MODEL slx_324b0836d6e7
KIND model
CONFIG AbsTol = auto
CONFIG EnableMultiTasking = on
CONFIG FixedStep = tS
CONFIG MaxStep = auto
CONFIG MinStep = auto
CONFIG RelTol = 1e-3
CONFIG SampleTimeConstraint = Unconstrained
CONFIG Solver = ode2
CONFIG SolverName = ode2
CONFIG StartTime = 0.0
CONFIG StopTime = inf
WORKSPACE source: MAT-file member
WORKSPACE m = 1000
BLOCK [BusSelector] Bus Selector
  OutputAsBus = off
  OutputSignals = RequestSteeringAngle_rad,RequestLongForce_N,RequestThrottle_perc,RequestBrake_bar,RequestGear
  Ports = [1, 5]
BLOCK [ModelReference] Model
  ModelNameDialog = debug_conversion_debug.slx
  ModelReferenceVersion = 1.8
  Ports = [1, 1]
BLOCK [ModelReference] Model1
  ModelNameDialog = debug_conversion_debug_slow.slx
  ModelReferenceVersion = 1.8
  Ports = [1, 1]
BLOCK [Terminator] Terminator
BLOCK [Terminator] Terminator1
BLOCK [Inport] in_ActuatorLimitations
  IconDisplay = Port number
  OutDataTypeStr = Bus: ActuatorLimitations
  Port = 4
BLOCK [Inport] in_ExternalDebug
  IconDisplay = Port number
  OutDataTypeStr = Bus: ExternalDebug
  Port = 5
BLOCK [Inport] in_TrajectoryPlanning
  IconDisplay = Port number
  OutDataTypeStr = Bus: TrajectoryPlanning
BLOCK [Inport] in_VehicleSensorData
  IconDisplay = Port number
  OutDataTypeStr = Bus: VehicleSensorData
  Port = 2
BLOCK [Inport] in_VehicleSystemStatus
  IconDisplay = Port number
  OutDataTypeStr = Bus: VehicleSystemStatus
  Port = 3
BLOCK [ModelReference] mvdc_vehicle_dynamics_control1
  ModelNameDialog = mvdc_vehicle_dynamics_control
  ModelReferenceVersion = 1.801
  Ports = [5, 8]
BLOCK [Outport] out_BrakePressure_bar
  IconDisplay = Port number
  Port = 9
BLOCK [Outport] out_Debug
  IconDisplay = Port number
  Port = 2
BLOCK [Outport] out_Debug_Slow
  IconDisplay = Port number
  Port = 3
BLOCK [Outport] out_Gear
  IconDisplay = Port number
  Port = 10
BLOCK [Outport] out_LiveVisualization_Send
  BusOutputAsStruct = on
  IconDisplay = Port number
  OutDataTypeStr = Bus: LiveVisualization
  Port = 6
  PortDimensions = 1
BLOCK [Outport] out_SteeringAngleAtWheel_rad
  IconDisplay = Port number
  Port = 4
BLOCK [Outport] out_TUMModeControl
  IconDisplay = Port number
  OutDataTypeStr = Bus: TUMModeControl
  Port = 7
BLOCK [Outport] out_ThrottlePosition_perc
  IconDisplay = Port number
  Port = 8
BLOCK [Outport] out_TractionForceSummedAtWheels_N
  IconDisplay = Port number
  Port = 5
BLOCK [Outport] out_VehicleDynamicState
  IconDisplay = Port number
  OutDataTypeStr = Bus: VehicleDynamicState
ANNOTATION (root): Author: Alexander Wischnewski (<email>) Chair of Automatic Control at TU Munich Description: This model uses the control software provided in vehicle dynamics control and maps it to the outputs required for a python wrapper class.
LINE Bus Selector:1 -> out_SteeringAngleAtWheel_rad:1
LINE Bus Selector:2 -> out_TractionForceSummedAtWheels_N:1
LINE Bus Selector:3 -> out_ThrottlePosition_perc:1
LINE Bus Selector:4 -> out_BrakePressure_bar:1
LINE Bus Selector:5 -> out_Gear:1
LINE Model1:1 -> out_Debug_Slow:1
LINE Model:1 -> out_Debug:1
LINE in_ActuatorLimitations:1 -> mvdc_vehicle_dynamics_control1:5
LINE in_ExternalDebug:1 -> mvdc_vehicle_dynamics_control1:2
LINE in_TrajectoryPlanning:1 -> mvdc_vehicle_dynamics_control1:1
LINE in_VehicleSensorData:1 -> mvdc_vehicle_dynamics_control1:3
LINE in_VehicleSystemStatus:1 -> mvdc_vehicle_dynamics_control1:4
LINE mvdc_vehicle_dynamics_control1:1 -> Model:1
LINE mvdc_vehicle_dynamics_control1:2 -> out_VehicleDynamicState:1
LINE mvdc_vehicle_dynamics_control1:3 -> out_TUMModeControl:1
LINE mvdc_vehicle_dynamics_control1:4 -> Terminator:1
LINE mvdc_vehicle_dynamics_control1:5 -> Bus Selector:1
LINE mvdc_vehicle_dynamics_control1:6 -> Terminator1:1
LINE mvdc_vehicle_dynamics_control1:7 -> Model1:1
LINE mvdc_vehicle_dynamics_control1:8 -> out_LiveVisualization_Send:1
